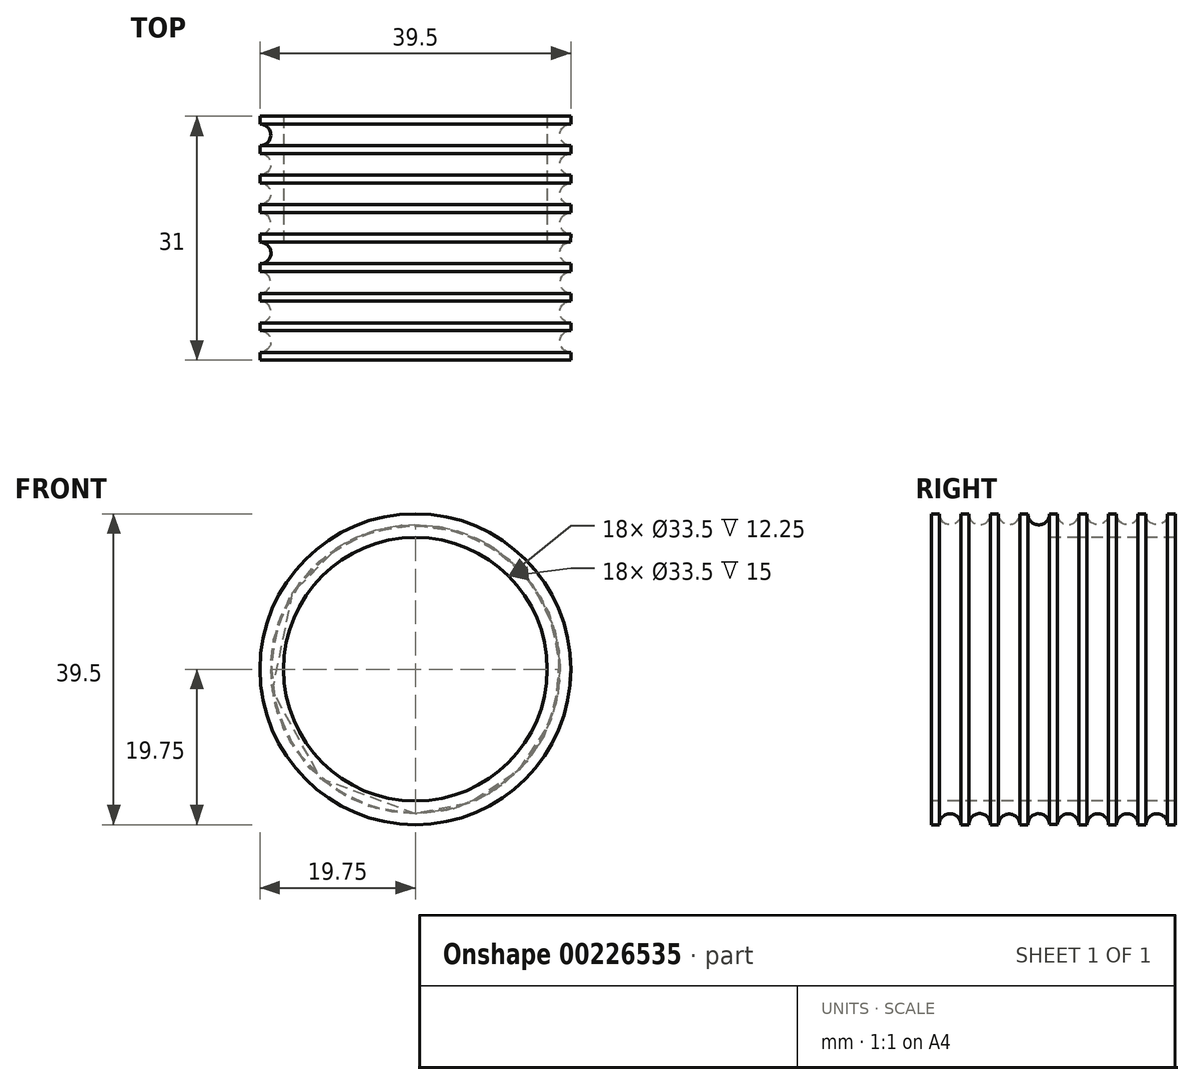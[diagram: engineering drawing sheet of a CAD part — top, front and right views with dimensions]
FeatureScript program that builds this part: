
annotation { "Feature Type Name" : "Feature", "Feature Type Description" : "" }
export const myFeature = defineFeature(function(context is Context, id is Id, definition is map)
    precondition{}
    {
        {
            var Q0;
            Q0=qCreatedBy(makeId("Top.planeOp"),FACE);
            var sketch = newSketch(context, id + "F0", { "sketchPlane" : qUnion([Q0])});
            skLineSegment(sketch, "E0", {"start": v(16.75, 0.5) * mm, "end": v(16.75, -2.26) * mm});
            skLineSegment(sketch, "E1", {"start": v(16.75, -2.26) * mm, "end": v(19.75, -2.26) * mm});
            skLineSegment(sketch, "E2", {"start": v(0, 0) * mm, "end": v(0, 7.6) * mm, "construction": true});
            skLineSegment(sketch, "E3", {"start": v(16.75, -2.26) * mm, "end": v(16.75, -6) * mm});
            skLineSegment(sketch, "E4", {"start": v(16.75, -6) * mm, "end": v(16.75, -9.76) * mm});
            skLineSegment(sketch, "E5", {"start": v(16.75, -14.5) * mm, "end": v(16.75, -9.76) * mm});
            skLineSegment(sketch, "E6", {"start": v(19.75, -2.26) * mm, "end": v(19.75, -3.26) * mm});
            skLineSegment(sketch, "E7", {"start": v(16.75, -6) * mm, "end": v(19.75, -6) * mm});
            skLineSegment(sketch, "E8", {"start": v(19.75, -6) * mm, "end": v(19.75, -7) * mm});
            skLineSegment(sketch, "E9", {"start": v(16.75, -9.76) * mm, "end": v(19.75, -9.76) * mm});
            skLineSegment(sketch, "E10", {"start": v(19.75, -9.76) * mm, "end": v(19.75, -10.76) * mm});
            skArc(sketch, "E11", {"start": v(19.75, -3.26) * mm, "mid": v(18.4, -4.63) * mm, "end": v(19.75, -6) * mm});
            skArc(sketch, "E12", {"start": v(19.75, -7) * mm, "mid": v(18.34, -8.38) * mm, "end": v(19.75, -9.76) * mm});
            skArc(sketch, "E13", {"start": v(19.75, -10.76) * mm, "mid": v(18.35, -12.13) * mm, "end": v(19.75, -13.5) * mm});
            skLineSegment(sketch, "E14", {"start": v(19.75, -13.5) * mm, "end": v(19.75, -14.5) * mm});
            skLineSegment(sketch, "E15", {"start": v(16.75, -14.5) * mm, "end": v(19.75, -14.5) * mm});
            skLineSegment(sketch, "E16", {"start": v(16.75, 0.5) * mm, "end": v(19.72, 0.5) * mm});
            skArc(sketch, "E17", {"start": v(19.72, 0.5) * mm, "mid": v(18.35, -0.9) * mm, "end": v(19.75, -2.26) * mm});
            skLineSegment(sketch, "E18", {"start": v(16.75, 4.24) * mm, "end": v(19.75, 4.24) * mm});
            skLineSegment(sketch, "E19", {"start": v(19.75, 4.24) * mm, "end": v(19.75, 4.24) * mm});
            skArc(sketch, "E20", {"start": v(19.75, 4.24) * mm, "mid": v(18.37, 2.87) * mm, "end": v(19.74, 1.5) * mm});
            skLineSegment(sketch, "E21", {"start": v(16.75, 4.24) * mm, "end": v(16.75, 8) * mm});
            skLineSegment(sketch, "E22", {"start": v(16.75, 8) * mm, "end": v(16.75, 11.74) * mm});
            skLineSegment(sketch, "E23", {"start": v(16.75, 11.74) * mm, "end": v(16.75, 16.5) * mm});
            skLineSegment(sketch, "E24", {"start": v(16.75, 8) * mm, "end": v(19.75, 8) * mm});
            skLineSegment(sketch, "E25", {"start": v(19.75, 8) * mm, "end": v(19.75, 8) * mm});
            skLineSegment(sketch, "E26", {"start": v(16.75, 11.74) * mm, "end": v(19.75, 11.74) * mm});
            skLineSegment(sketch, "E27", {"start": v(16.75, 16.5) * mm, "end": v(19.75, 16.5) * mm});
            skLineSegment(sketch, "E28", {"start": v(19.75, 11.74) * mm, "end": v(19.75, 12.74) * mm});
            skArc(sketch, "E29", {"start": v(19.75, 15.5) * mm, "mid": v(18.36, 14.12) * mm, "end": v(19.75, 12.74) * mm});
            skArc(sketch, "E30", {"start": v(19.75, 8) * mm, "mid": v(18.37, 6.62) * mm, "end": v(19.75, 5.24) * mm});
            skLineSegment(sketch, "E31", {"start": v(19.75, 5.24) * mm, "end": v(19.75, 4.24) * mm});
            skLineSegment(sketch, "E32", {"start": v(19.75, 9) * mm, "end": v(19.75, 8) * mm});
            skLineSegment(sketch, "E33", {"start": v(19.75, 16.5) * mm, "end": v(19.75, 15.5) * mm});
            skLineSegment(sketch, "E34", {"start": v(16.75, 4.24) * mm, "end": v(16.75, 0.5) * mm});
            skLineSegment(sketch, "E35", {"start": v(19.74, 1.5) * mm, "end": v(19.72, 0.5) * mm});
            skArc(sketch, "E36", {"start": v(19.75, 11.74) * mm, "mid": v(18.37, 10.37) * mm, "end": v(19.75, 9) * mm});
            skLineSegment(sketch, "E37", {"start": v(0, 0) * mm, "end": v(16.75, 0) * mm});
            skSolve(sketch);
        }
        {
            var Q0;
            Q0 = qSketchRegion(id + "F0", true);
            var Q1;
            Q1=makeQuery(id+"F0.imprint","IMPRINT",FACE,{"disambiguationData":[TD([[makeQuery(id+"F0.imprint","IMPRINT",EDGE,{"derivedFrom":sQuery(id+"F0.wireOp",EDGE,"NVE6DKzE-0QpP-bYCF-STc0-ITq78N2TTr6M")}),1.0]])]});
            var Q2;
            Q2=makeQuery(id+"F0.imprint","IMPRINT",FACE,{"disambiguationData":[TD([[makeQuery(id+"F0.imprint","IMPRINT",EDGE,{"derivedFrom":sQuery(id+"F0.wireOp",EDGE,"XOsZPx7i-W7u0-B1XT-LP0v-g57uoqOJnjVY")}),-1.0]])]});
            var Q3;
            Q3=makeQuery(id+"F0.imprint","IMPRINT",FACE,{"disambiguationData":[TD([[makeQuery(id+"F0.imprint","IMPRINT",EDGE,{"derivedFrom":sQuery(id+"F0.wireOp",EDGE,"ikBf3zxj-2eLJ-35q3-Ysip-J7iZRBvFPbNc")}),-1.0]])]});
            var Q4;
            Q4=makeQuery(id+"F0.imprint","IMPRINT",FACE,{"disambiguationData":[TD([[makeQuery(id+"F0.imprint","IMPRINT",EDGE,{"derivedFrom":sQuery(id+"F0.wireOp",EDGE,"lufvvvDV-jcgL-W5i5-nA09-cOKmf1cOH8tZ")}),-1.0]])]});
            var Q5;
            Q5=makeQuery(id+"F0.imprint","IMPRINT",FACE,{"disambiguationData":[TD([[makeQuery(id+"F0.imprint","IMPRINT",EDGE,{"derivedFrom":sQuery(id+"F0.wireOp",EDGE,"E0")}),1.0]])]});
            var Q6;
            Q6=makeQuery(id+"F0.imprint","IMPRINT",FACE,{"disambiguationData":[TD([[makeQuery(id+"F0.imprint","IMPRINT",EDGE,{"derivedFrom":sQuery(id+"F0.wireOp",EDGE,"E4")}),1.0]])]});
            var Q7;
            Q7=makeQuery(id+"F0.imprint","IMPRINT",FACE,{"disambiguationData":[TD([[makeQuery(id+"F0.imprint","IMPRINT",EDGE,{"derivedFrom":sQuery(id+"F0.wireOp",EDGE,"E5")}),-1.0]])]});
            var Q8;
            Q8=makeQuery(id+"F0.imprint","IMPRINT",FACE,{"disambiguationData":[TD([[makeQuery(id+"F0.imprint","IMPRINT",EDGE,{"derivedFrom":sQuery(id+"F0.wireOp",EDGE,"E1")}),-1.0]])]});
            var Q9;
            Q9=sQuery(id+"F0.wireOp",EDGE,"E2");
            revolve(context, id + "F1", {"entities" : qUnion([Q0, Q1, Q2, Q3, Q4, Q5, Q6, Q7, Q8]), "axis" : qUnion([Q9]), "revolveType" : RevolveType.FULL});
        }
    });
